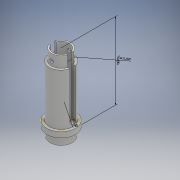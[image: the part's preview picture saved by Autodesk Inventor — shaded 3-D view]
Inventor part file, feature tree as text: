
AUTODESK INVENTOR PART (.ipt)
format: ipt  version: 2018 (Build 220112000, 112)  size: 195,072 bytes
history: native  units: mm
features: extrude x7, sketch x7, other x5, fillet x1
ambient origin geometry x8: Origin, YZ Plane, XZ Plane, XY Plane, X Axis, Y Axis, Z Axis, Center Point
bodies: Solide1 (feature_tree)
feature tree (20):
  other  "Annotations"
  extrude  "Extrusion1"  Depth=17.5mm
  extrude  "Extrusion2"  Depth=15.0mm
  extrude  "Extrusion3"  Depth=10.0mm TaperAngle=0.0deg
  other  "Plan de construction1"
  extrude  "Extrusion4"  Depth=21.5mm
  extrude  "Extrusion5"  Depth=60.0mm TaperAngle=0.0deg
  fillet  "Congé1"  Radius=15.0mm
  extrude  "Extrusion6"  Depth=60.0mm TaperAngle=0.0deg
  extrude  "Extrusion7"  [1 undecoded]
  sketch  "Esquisse1"
  sketch  "Esquisse2"
  sketch  "Esquisse3"
  sketch  "Esquisse4"
  sketch  "Esquisse5"
  sketch  "Esquisse6"
  sketch  "Esquisse8"
  other  "Cote linéaire 1"
  other  "Cote de diamètre 1"
  other  "Cote de rayon 1"
note: 1 required parameter value undecoded (feature->parameter linkage not recoverable at this tier; creation-order binding heuristic only, values carry confidence <= 0.55)
